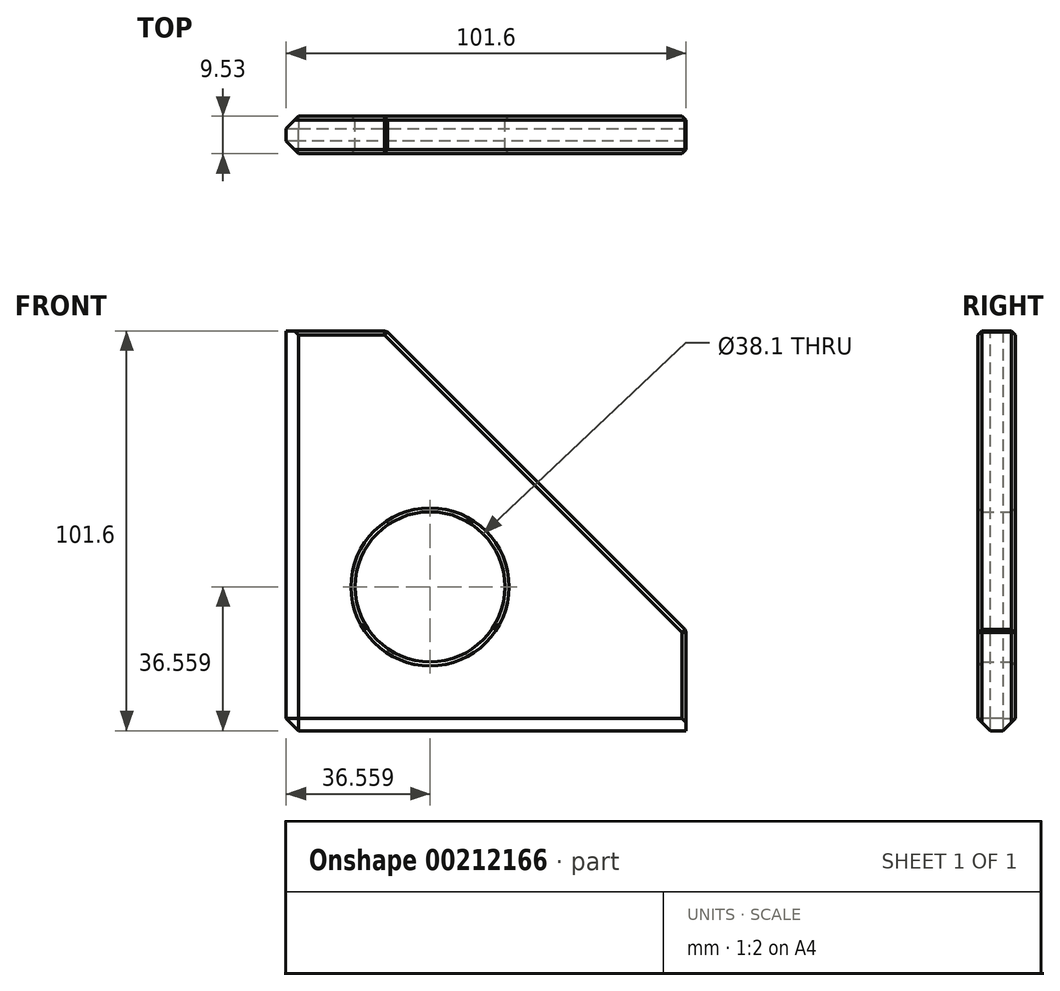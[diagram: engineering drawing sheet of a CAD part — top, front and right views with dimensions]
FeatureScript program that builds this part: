
annotation { "Feature Type Name" : "Feature", "Feature Type Description" : "" }
export const myFeature = defineFeature(function(context is Context, id is Id, definition is map)
    precondition{}
    {
        {
            var Q0;
            Q0=qCreatedBy(makeId("Front.planeOp"),FACE);
            var sketch = newSketch(context, id + "F0", { "sketchPlane" : qUnion([Q0])});
            skLineSegment(sketch, "E0", {"start": v(0, 0) * mm, "end": v(0, 101.6) * mm});
            skLineSegment(sketch, "E1", {"start": v(0, 101.6) * mm, "end": v(25.4, 101.6) * mm});
            skLineSegment(sketch, "E2", {"start": v(25.4, 101.6) * mm, "end": v(101.6, 25.4) * mm});
            skLineSegment(sketch, "E3", {"start": v(101.6, 25.4) * mm, "end": v(101.6, 0) * mm});
            skLineSegment(sketch, "E4", {"start": v(101.6, 0) * mm, "end": v(0, 0) * mm});
            skCircle(sketch, "E5", {"center": v(36.56, 36.56) * mm, "radius": 19.05 * mm});
            skSolve(sketch);
        }
        {
            var Q0;
            Q0=makeQuery(id+"F0.imprint","IMPRINT",FACE,{"disambiguationData":[TD([[makeQuery(id+"F0.imprint","IMPRINT",EDGE,{"derivedFrom":sQuery(id+"F0.wireOp",EDGE,"E0")}),-1.0]])]});
            extrude(context, id + "F1", {"entities" : qUnion([Q0]), "depth" : 9.52 * mm});
        }
        {
            var Q0;
            Q0=makeQuery(id+"F1.opExtrude","SWEPT_FACE",FACE,{"disambiguationData":[OSD([sQuery(id+"F0.wireOp",EDGE,"E5")])]});
            var Q1;
            Q1=makeQuery(id+"F1.opExtrude","SWEPT_FACE",FACE,{"disambiguationData":[OSD([sQuery(id+"F0.wireOp",EDGE,"E2")])]});
            var Q2;
            Q2=makeQuery(id+"F1.opExtrude","CAP_EDGE",EDGE,{"disambiguationData":[OSD([sQuery(id+"F0.wireOp",EDGE,"E1")])],"isStart":true});
            var Q3;
            Q3=makeQuery(id+"F1.opExtrude","CAP_EDGE",EDGE,{"disambiguationData":[OSD([sQuery(id+"F0.wireOp",EDGE,"E1")])],"isStart":false});
            var Q4;
            Q4=makeQuery(id+"F1.opExtrude","CAP_EDGE",EDGE,{"disambiguationData":[OSD([sQuery(id+"F0.wireOp",EDGE,"E3")])],"isStart":true});
            var Q5;
            Q5=makeQuery(id+"F1.opExtrude","CAP_EDGE",EDGE,{"disambiguationData":[OSD([sQuery(id+"F0.wireOp",EDGE,"E3")])],"isStart":false});
            chamfer(context, id + "F2", {"entities" : qUnion([Q0, Q1, Q2, Q3, Q4, Q5]), "width" : 1.02 * mm, "tangentPropagation" : true});
        }
        {
            var Q0;
            Q0=makeQuery(id+"F1.opExtrude","SWEPT_EDGE",EDGE,{"disambiguationData":[OSD([sQuery(id+"F0.wireOp",EDGE,"E0"),sQuery(id+"F0.wireOp",EDGE,"E4")])]});
            var Q1;
            Q1=makeQuery(id+"F1.opExtrude","CAP_EDGE",EDGE,{"disambiguationData":[OSD([sQuery(id+"F0.wireOp",EDGE,"E0")])],"isStart":true});
            var Q2;
            Q2=makeQuery(id+"F1.opExtrude","CAP_EDGE",EDGE,{"disambiguationData":[OSD([sQuery(id+"F0.wireOp",EDGE,"E0")])],"isStart":false});
            var Q3;
            Q3=makeQuery(id+"F1.opExtrude","CAP_EDGE",EDGE,{"disambiguationData":[OSD([sQuery(id+"F0.wireOp",EDGE,"E4")])],"isStart":true});
            var Q4;
            Q4=makeQuery(id+"F1.opExtrude","CAP_EDGE",EDGE,{"disambiguationData":[OSD([sQuery(id+"F0.wireOp",EDGE,"E4")])],"isStart":false});
            chamfer(context, id + "F3", {"entities" : qUnion([Q0, Q1, Q2, Q3, Q4]), "width" : 3.17 * mm, "tangentPropagation" : true});
        }
    });
